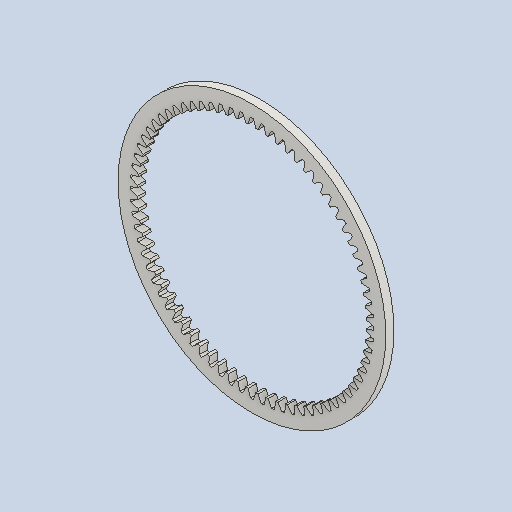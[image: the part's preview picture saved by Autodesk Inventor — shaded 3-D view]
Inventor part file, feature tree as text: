
AUTODESK INVENTOR PART (.ipt)
format: ipt  version: 2024 (Build 280153000, 153)  size: 406,016 bytes
history: native  units: mm (DEFAULTED — no unit token found)
features: plane x3, other x3, extrude x1, sketch x1
ambient origin geometry x8: Origin, YZ Plane, XZ Plane, XY Plane, X Axis, Y Axis, Z Axis, Center Point
bodies: Solid1 (feature_tree)
feature tree (8):
  extrude  "Extrusion1"  Depth=5.0mm TaperAngle=0.0deg
  plane  "Work Plane2"
  plane  "Work Plane8"
  plane  "Work Plane9"
  other  "Spur Gear"
  sketch  "Sketch1"  dims[d0=163.9mm d1=5.0mm d2=0.0mm d3=144.0mm d4=10.0mm d5=0.0mm d16=54.0mm d17=0.0mm d34=0.436332mm d39=0.0mm d45=0.0mm d47=54.0mm d50=0.0mm d51=0.0mm d52=54.0mm]
  other  "Srf1"
  other  "Pitch Diameter"
